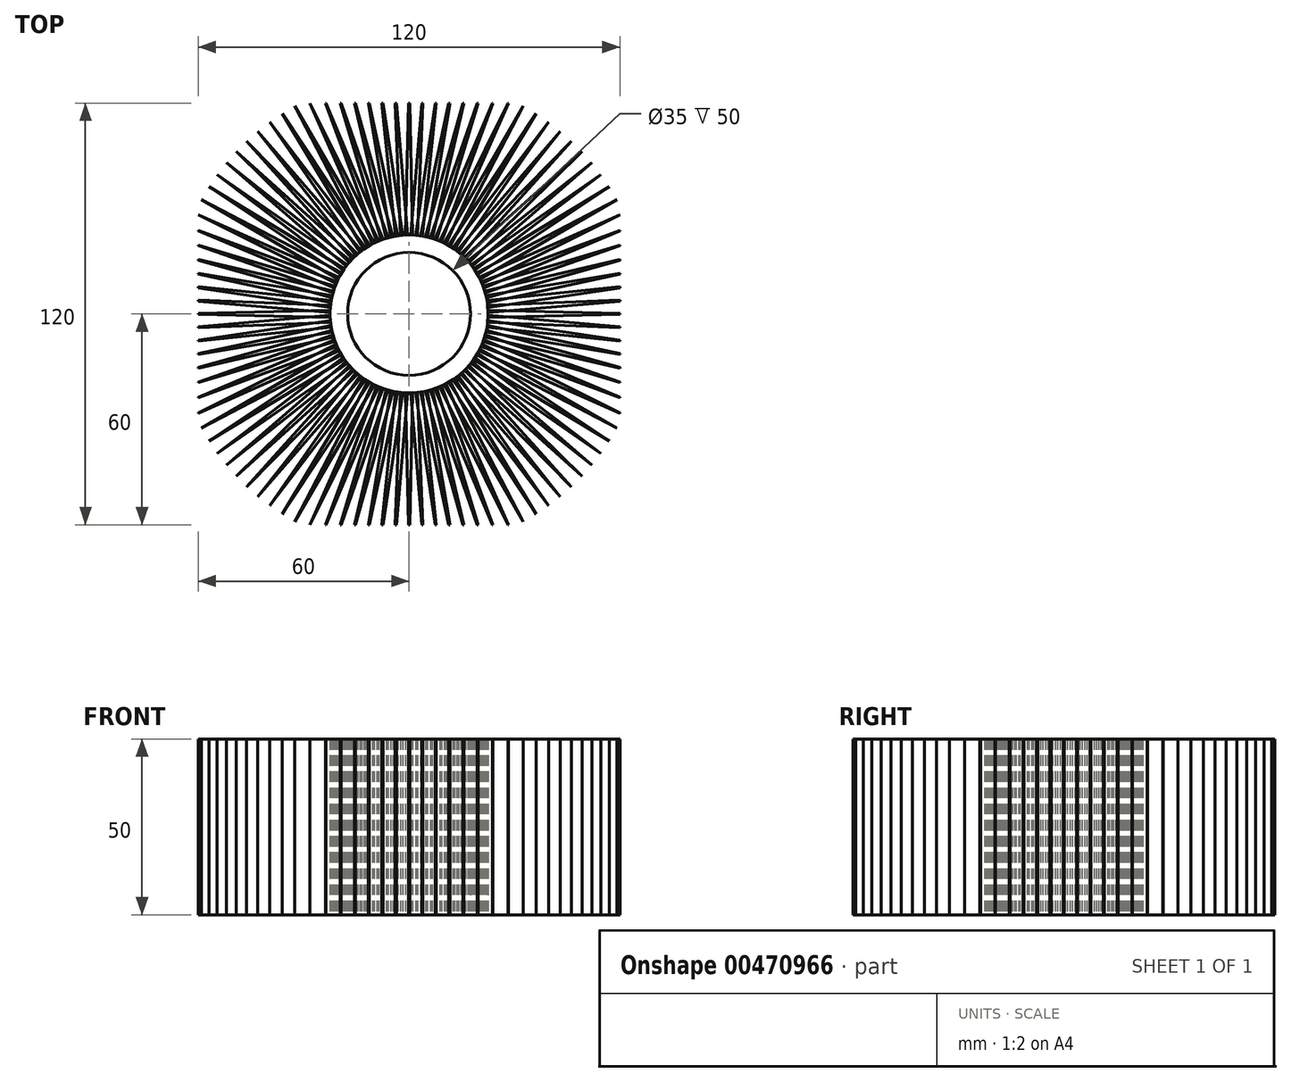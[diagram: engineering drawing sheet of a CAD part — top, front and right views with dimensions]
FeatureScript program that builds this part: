
annotation { "Feature Type Name" : "Feature", "Feature Type Description" : "" }
export const myFeature = defineFeature(function(context is Context, id is Id, definition is map)
    precondition{}
    {
        {
            var Q0;
            Q0=qCreatedBy(makeId("Top.planeOp"),FACE);
            var sketch = newSketch(context, id + "F0", { "sketchPlane" : qUnion([Q0])});
            skCircle(sketch, "E0", {"center": v(0, 0) * mm, "radius": 17.5 * mm});
            skCircle(sketch, "E1", {"center": v(0, 0) * mm, "radius": 22.5 * mm});
            skSolve(sketch);
        }
        {
            var Q0;
            Q0=makeQuery(id+"F0.imprint","IMPRINT",FACE,{"disambiguationData":[TD([[makeQuery(id+"F0.imprint","IMPRINT",EDGE,{"derivedFrom":sQuery(id+"F0.wireOp",EDGE,"E0")}),-1.0]])]});
            extrude(context, id + "F1", {"entities" : qUnion([Q0]), "depth" : 50 * mm});
        }
        {
            var Q0;
            Q0=qCreatedBy(makeId("Top.planeOp"),FACE);
            var sketch = newSketch(context, id + "F2", { "sketchPlane" : qUnion([Q0])});
            skLineSegment(sketch, "E2", {"start": v(-1, 22.48) * mm, "end": v(0, 67.5) * mm});
            skLineSegment(sketch, "E3", {"start": v(0, 67.5) * mm, "end": v(1, 22.48) * mm});
            skLineSegment(sketch, "E4", {"start": v(-1, 22.48) * mm, "end": v(1, 22.48) * mm});
            skLineSegment(sketch, "E5.1.0", {"start": v(-8.46, 66.97) * mm, "end": v(-1.83, 22.43) * mm});
            skLineSegment(sketch, "E5.2.0", {"start": v(-16.79, 65.38) * mm, "end": v(-4.62, 22.02) * mm});
            skLineSegment(sketch, "E5.3.0", {"start": v(-24.85, 62.76) * mm, "end": v(-7.34, 21.27) * mm});
            skLineSegment(sketch, "E5.4.0", {"start": v(-32.52, 59.15) * mm, "end": v(-9.95, 20.18) * mm});
            skLineSegment(sketch, "E5.5.0", {"start": v(-39.68, 54.6) * mm, "end": v(-12.4, 18.77) * mm});
            skLineSegment(sketch, "E5.6.0", {"start": v(-46.2, 49.2) * mm, "end": v(-14.66, 17.07) * mm});
            skLineSegment(sketch, "E5.7.0", {"start": v(-52, 43.03) * mm, "end": v(-16.68, 15.1) * mm});
            skLineSegment(sketch, "E5.8.0", {"start": v(-57, 36.17) * mm, "end": v(-18.44, 12.89) * mm});
            skLineSegment(sketch, "E5.9.0", {"start": v(-61.08, 28.74) * mm, "end": v(-19.91, 10.48) * mm});
            skLineSegment(sketch, "E5.10.0", {"start": v(-64.2, 20.86) * mm, "end": v(-21.07, 7.9) * mm});
            skLineSegment(sketch, "E5.11.0", {"start": v(-66.3, 12.65) * mm, "end": v(-21.9, 5.2) * mm});
            skLineSegment(sketch, "E5.12.0", {"start": v(-67.37, 4.24) * mm, "end": v(-22.37, 2.4) * mm});
            skLineSegment(sketch, "E5.13.0", {"start": v(-67.37, -4.24) * mm, "end": v(-22.5, -0.41) * mm});
            skLineSegment(sketch, "E5.14.0", {"start": v(-66.3, -12.65) * mm, "end": v(-22.27, -3.23) * mm});
            skLineSegment(sketch, "E5.15.0", {"start": v(-64.2, -20.86) * mm, "end": v(-21.69, -6) * mm});
            skLineSegment(sketch, "E5.16.0", {"start": v(-61.08, -28.74) * mm, "end": v(-20.76, -8.67) * mm});
            skLineSegment(sketch, "E5.17.0", {"start": v(-57, -36.17) * mm, "end": v(-19.51, -11.2) * mm});
            skLineSegment(sketch, "E5.18.0", {"start": v(-52, -43.03) * mm, "end": v(-17.96, -13.56) * mm});
            skLineSegment(sketch, "E5.19.0", {"start": v(-46.2, -49.2) * mm, "end": v(-16.12, -15.7) * mm});
            skLineSegment(sketch, "E5.20.0", {"start": v(-39.68, -54.6) * mm, "end": v(-14.02, -17.6) * mm});
            skLineSegment(sketch, "E5.21.0", {"start": v(-32.52, -59.15) * mm, "end": v(-11.7, -19.22) * mm});
            skLineSegment(sketch, "E5.22.0", {"start": v(-24.85, -62.76) * mm, "end": v(-9.2, -20.53) * mm});
            skLineSegment(sketch, "E5.23.0", {"start": v(-16.79, -65.38) * mm, "end": v(-6.56, -21.52) * mm});
            skLineSegment(sketch, "E5.24.0", {"start": v(-8.46, -66.97) * mm, "end": v(-3.8, -22.18) * mm});
            skLineSegment(sketch, "E5.25.0", {"start": v(0, -67.5) * mm, "end": v(-1, -22.48) * mm});
            skLineSegment(sketch, "E5.26.0", {"start": v(8.46, -66.97) * mm, "end": v(1.83, -22.43) * mm});
            skLineSegment(sketch, "E5.27.0", {"start": v(16.79, -65.38) * mm, "end": v(4.62, -22.02) * mm});
            skLineSegment(sketch, "E5.28.0", {"start": v(24.85, -62.76) * mm, "end": v(7.34, -21.27) * mm});
            skLineSegment(sketch, "E5.29.0", {"start": v(32.52, -59.15) * mm, "end": v(9.95, -20.18) * mm});
            skLineSegment(sketch, "E5.30.0", {"start": v(39.68, -54.6) * mm, "end": v(12.4, -18.77) * mm});
            skLineSegment(sketch, "E5.31.0", {"start": v(46.2, -49.2) * mm, "end": v(14.66, -17.07) * mm});
            skLineSegment(sketch, "E5.32.0", {"start": v(52, -43.03) * mm, "end": v(16.68, -15.1) * mm});
            skLineSegment(sketch, "E5.33.0", {"start": v(57, -36.17) * mm, "end": v(18.44, -12.89) * mm});
            skLineSegment(sketch, "E5.34.0", {"start": v(61.08, -28.74) * mm, "end": v(19.91, -10.48) * mm});
            skLineSegment(sketch, "E5.35.0", {"start": v(64.2, -20.86) * mm, "end": v(21.07, -7.9) * mm});
            skLineSegment(sketch, "E5.36.0", {"start": v(66.3, -12.65) * mm, "end": v(21.9, -5.2) * mm});
            skLineSegment(sketch, "E5.37.0", {"start": v(67.37, -4.24) * mm, "end": v(22.37, -2.4) * mm});
            skLineSegment(sketch, "E5.38.0", {"start": v(67.37, 4.24) * mm, "end": v(22.5, 0.41) * mm});
            skLineSegment(sketch, "E5.39.0", {"start": v(66.3, 12.65) * mm, "end": v(22.27, 3.23) * mm});
            skLineSegment(sketch, "E5.40.0", {"start": v(64.2, 20.86) * mm, "end": v(21.69, 6) * mm});
            skLineSegment(sketch, "E5.41.0", {"start": v(61.08, 28.74) * mm, "end": v(20.76, 8.67) * mm});
            skLineSegment(sketch, "E5.42.0", {"start": v(57, 36.17) * mm, "end": v(19.51, 11.2) * mm});
            skLineSegment(sketch, "E5.43.0", {"start": v(52, 43.03) * mm, "end": v(17.96, 13.56) * mm});
            skLineSegment(sketch, "E5.44.0", {"start": v(46.2, 49.2) * mm, "end": v(16.12, 15.7) * mm});
            skLineSegment(sketch, "E5.45.0", {"start": v(39.68, 54.6) * mm, "end": v(14.02, 17.6) * mm});
            skLineSegment(sketch, "E5.46.0", {"start": v(32.52, 59.15) * mm, "end": v(11.7, 19.22) * mm});
            skLineSegment(sketch, "E5.47.0", {"start": v(24.85, 62.76) * mm, "end": v(9.2, 20.53) * mm});
            skLineSegment(sketch, "E5.48.0", {"start": v(16.79, 65.38) * mm, "end": v(6.56, 21.52) * mm});
            skLineSegment(sketch, "E5.49.0", {"start": v(8.46, 66.97) * mm, "end": v(3.8, 22.18) * mm});
            skPoint(sketch, "E5.center", {"position": v(0, 0) * mm});
            skLineSegment(sketch, "E6.1.0", {"start": v(-3.8, 22.18) * mm, "end": v(-8.46, 66.97) * mm});
            skLineSegment(sketch, "E6.2.0", {"start": v(-6.56, 21.52) * mm, "end": v(-16.79, 65.38) * mm});
            skLineSegment(sketch, "E6.3.0", {"start": v(-9.2, 20.53) * mm, "end": v(-24.85, 62.76) * mm});
            skLineSegment(sketch, "E6.4.0", {"start": v(-11.7, 19.22) * mm, "end": v(-32.52, 59.15) * mm});
            skLineSegment(sketch, "E6.5.0", {"start": v(-14.02, 17.6) * mm, "end": v(-39.68, 54.6) * mm});
            skLineSegment(sketch, "E6.6.0", {"start": v(-16.12, 15.7) * mm, "end": v(-46.2, 49.2) * mm});
            skLineSegment(sketch, "E6.7.0", {"start": v(-17.96, 13.56) * mm, "end": v(-52, 43.03) * mm});
            skLineSegment(sketch, "E6.8.0", {"start": v(-19.51, 11.2) * mm, "end": v(-57, 36.17) * mm});
            skLineSegment(sketch, "E6.9.0", {"start": v(-20.76, 8.67) * mm, "end": v(-61.08, 28.74) * mm});
            skLineSegment(sketch, "E6.10.0", {"start": v(-21.69, 6) * mm, "end": v(-64.2, 20.86) * mm});
            skLineSegment(sketch, "E6.11.0", {"start": v(-22.27, 3.23) * mm, "end": v(-66.3, 12.65) * mm});
            skLineSegment(sketch, "E6.12.0", {"start": v(-22.5, 0.41) * mm, "end": v(-67.37, 4.24) * mm});
            skLineSegment(sketch, "E6.13.0", {"start": v(-22.37, -2.4) * mm, "end": v(-67.37, -4.24) * mm});
            skLineSegment(sketch, "E6.14.0", {"start": v(-21.9, -5.2) * mm, "end": v(-66.3, -12.65) * mm});
            skLineSegment(sketch, "E6.15.0", {"start": v(-21.07, -7.9) * mm, "end": v(-64.2, -20.86) * mm});
            skLineSegment(sketch, "E6.16.0", {"start": v(-19.91, -10.48) * mm, "end": v(-61.08, -28.74) * mm});
            skLineSegment(sketch, "E6.17.0", {"start": v(-18.44, -12.89) * mm, "end": v(-57, -36.17) * mm});
            skLineSegment(sketch, "E6.18.0", {"start": v(-16.68, -15.1) * mm, "end": v(-52, -43.03) * mm});
            skLineSegment(sketch, "E6.19.0", {"start": v(-14.66, -17.07) * mm, "end": v(-46.2, -49.2) * mm});
            skLineSegment(sketch, "E6.20.0", {"start": v(-12.4, -18.77) * mm, "end": v(-39.68, -54.6) * mm});
            skLineSegment(sketch, "E6.21.0", {"start": v(-9.95, -20.18) * mm, "end": v(-32.52, -59.15) * mm});
            skLineSegment(sketch, "E6.22.0", {"start": v(-7.34, -21.27) * mm, "end": v(-24.85, -62.76) * mm});
            skLineSegment(sketch, "E6.23.0", {"start": v(-4.62, -22.02) * mm, "end": v(-16.79, -65.38) * mm});
            skLineSegment(sketch, "E6.24.0", {"start": v(-1.83, -22.43) * mm, "end": v(-8.46, -66.97) * mm});
            skLineSegment(sketch, "E6.25.0", {"start": v(1, -22.48) * mm, "end": v(0, -67.5) * mm});
            skLineSegment(sketch, "E6.26.0", {"start": v(3.8, -22.18) * mm, "end": v(8.46, -66.97) * mm});
            skLineSegment(sketch, "E6.27.0", {"start": v(6.56, -21.52) * mm, "end": v(16.79, -65.38) * mm});
            skLineSegment(sketch, "E6.28.0", {"start": v(9.2, -20.53) * mm, "end": v(24.85, -62.76) * mm});
            skLineSegment(sketch, "E6.29.0", {"start": v(11.7, -19.22) * mm, "end": v(32.52, -59.15) * mm});
            skLineSegment(sketch, "E6.30.0", {"start": v(14.02, -17.6) * mm, "end": v(39.68, -54.6) * mm});
            skLineSegment(sketch, "E6.31.0", {"start": v(16.12, -15.7) * mm, "end": v(46.2, -49.2) * mm});
            skLineSegment(sketch, "E6.32.0", {"start": v(17.96, -13.56) * mm, "end": v(52, -43.03) * mm});
            skLineSegment(sketch, "E6.33.0", {"start": v(19.51, -11.2) * mm, "end": v(57, -36.17) * mm});
            skLineSegment(sketch, "E6.34.0", {"start": v(20.76, -8.67) * mm, "end": v(61.08, -28.74) * mm});
            skLineSegment(sketch, "E6.35.0", {"start": v(21.69, -6) * mm, "end": v(64.2, -20.86) * mm});
            skLineSegment(sketch, "E6.36.0", {"start": v(22.27, -3.23) * mm, "end": v(66.3, -12.65) * mm});
            skLineSegment(sketch, "E6.37.0", {"start": v(22.5, -0.41) * mm, "end": v(67.37, -4.24) * mm});
            skLineSegment(sketch, "E6.38.0", {"start": v(22.37, 2.4) * mm, "end": v(67.37, 4.24) * mm});
            skLineSegment(sketch, "E6.39.0", {"start": v(21.9, 5.2) * mm, "end": v(66.3, 12.65) * mm});
            skLineSegment(sketch, "E6.40.0", {"start": v(21.07, 7.9) * mm, "end": v(64.2, 20.86) * mm});
            skLineSegment(sketch, "E6.41.0", {"start": v(19.91, 10.48) * mm, "end": v(61.08, 28.74) * mm});
            skLineSegment(sketch, "E6.42.0", {"start": v(18.44, 12.89) * mm, "end": v(57, 36.17) * mm});
            skLineSegment(sketch, "E6.43.0", {"start": v(16.68, 15.1) * mm, "end": v(52, 43.03) * mm});
            skLineSegment(sketch, "E6.44.0", {"start": v(14.66, 17.07) * mm, "end": v(46.2, 49.2) * mm});
            skLineSegment(sketch, "E6.45.0", {"start": v(12.4, 18.77) * mm, "end": v(39.68, 54.6) * mm});
            skLineSegment(sketch, "E6.46.0", {"start": v(9.95, 20.18) * mm, "end": v(32.52, 59.15) * mm});
            skLineSegment(sketch, "E6.47.0", {"start": v(7.34, 21.27) * mm, "end": v(24.85, 62.76) * mm});
            skLineSegment(sketch, "E6.48.0", {"start": v(4.62, 22.02) * mm, "end": v(16.79, 65.38) * mm});
            skLineSegment(sketch, "E6.49.0", {"start": v(1.83, 22.43) * mm, "end": v(8.46, 66.97) * mm});
            skSolve(sketch);
        }
        {
            var Q0;
            Q0 = qSketchRegion(id + "F2", true);
            extrude(context, id + "F3", {"entities" : qUnion([Q0]), "depth" : 50 * mm});
        }
        {
            var Q0;
            Q0=makeQuery(id+"F3.opExtrude","SWEPT_BODY",BODY,{"disambiguationData":[OSD([sQuery(id+"F2.wireOp",EDGE,"E2"),sQuery(id+"F2.wireOp",EDGE,"E3"),sQuery(id+"F2.wireOp",EDGE,"E4")])]});
            var Q1;
            Q1=makeQuery(id+"F1.opExtrude","CAP_EDGE",EDGE,{"disambiguationData":[OSD([sQuery(id+"F0.wireOp",EDGE,"E0")])],"isStart":true});
            circularPattern(context, id + "F4", {"entities" : qUnion([Q0]), "axis" : qUnion([Q1]), "angle" : 360 * degree, "instanceCount" : 100, "equalSpace" : true});
        }
        {
            var Q0;
            Q0 = qSketchRegion(id + "F2", true);
            var sketch = newSketch(context, id + "F5", { "sketchPlane" : qUnion([Q0])});
            skLineSegment(sketch, "E7.bottom", {"start": v(-60, 60) * mm, "end": v(60, 60) * mm});
            skLineSegment(sketch, "E7.top", {"start": v(-60, -60) * mm, "end": v(60, -60) * mm});
            skLineSegment(sketch, "E7.left", {"start": v(-60, 60) * mm, "end": v(-60, -60) * mm});
            skLineSegment(sketch, "E7.right", {"start": v(60, 60) * mm, "end": v(60, -60) * mm});
            skSolve(sketch);
        }
        {
            var Q0;
            Q0 = qSketchRegion(id + "F5", true);
            extrude(context, id + "F6", {"entities" : qUnion([Q0]), "operationType" : NewBodyOperationType.INTERSECT, "endBound" : BoundingType.THROUGH_ALL, "depth" : 25 * mm, "offsetDistance" : 25 * mm});
        }
    });
